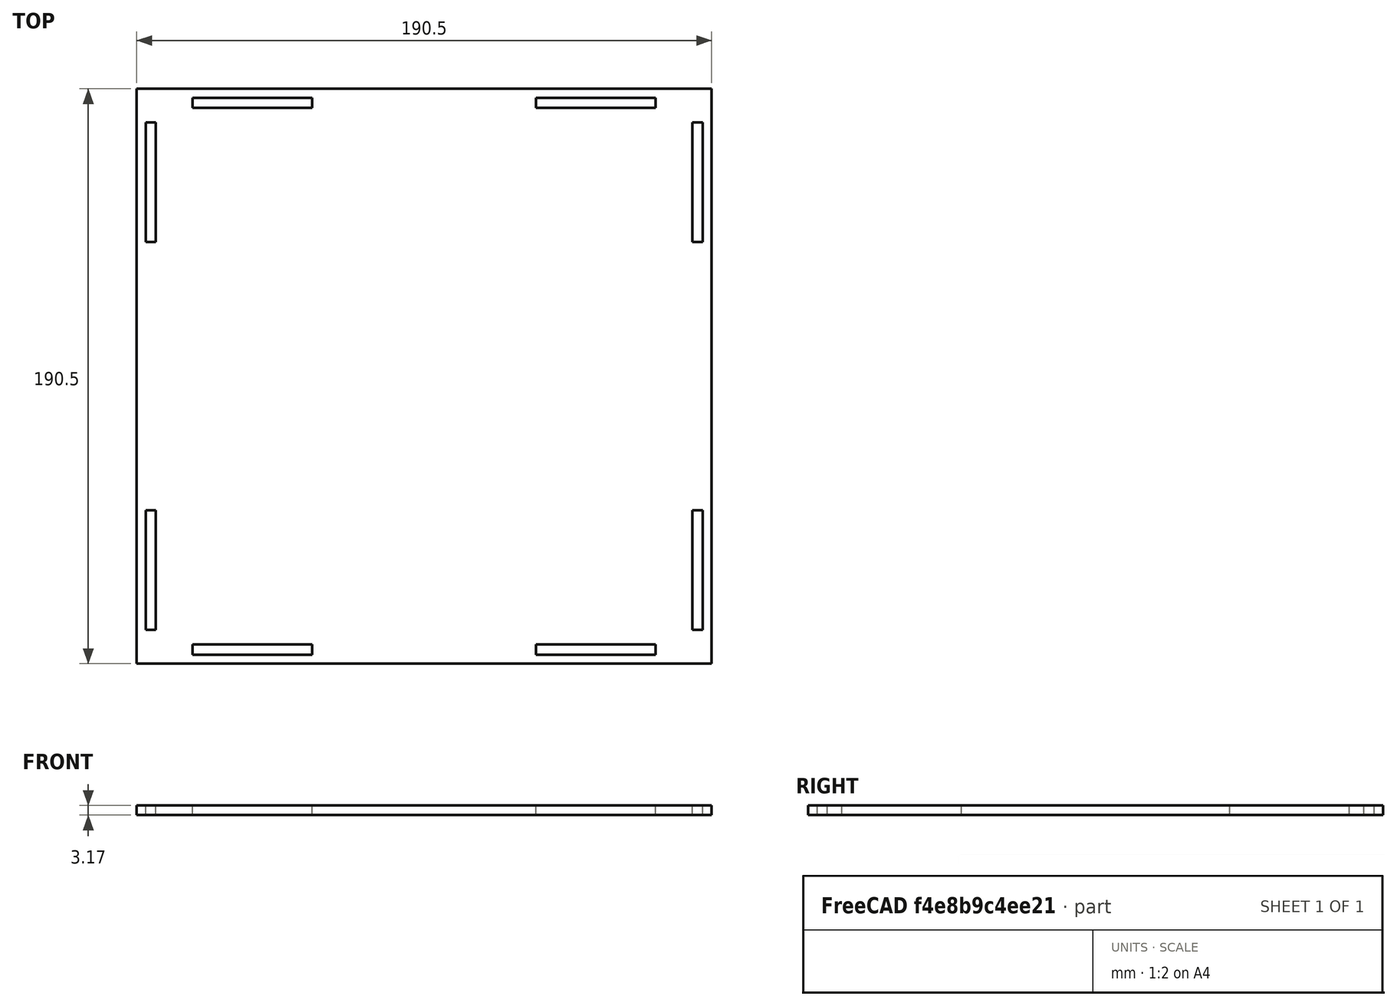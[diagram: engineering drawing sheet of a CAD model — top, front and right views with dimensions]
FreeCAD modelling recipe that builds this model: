
FCSTD DOCUMENT  (FreeCAD 0.18R4 (GitTag))
Label: tpr68k
License: All rights reserved
LicenseURL: http://en.wikipedia.org/wiki/All_rights_reserved
objects: Sketcher::SketchObject×1, PartDesign::Pad×1, PartDesign::Body×1, App::Part×1, Mesh::Feature×1
note: 4 computed .brp shape members not serialized (recipe doc carries the construction recipe); baked Part::Feature solids carry a one-line shape summary decoded from their .brp

FEATURE [Sketcher::SketchObject] Sketch
  MapMode = 5
  Support = -> [XY_Plane001]
  sketch-geometry (36):
    g0: LineSegment StartX=-95.25 StartY=95.25 StartZ=0 EndX=95.25 EndY=95.25 EndZ=0
    g1: LineSegment StartX=95.25 StartY=95.25 StartZ=0 EndX=95.25 EndY=-95.25 EndZ=0
    g2: LineSegment StartX=95.25 StartY=-95.25 StartZ=0 EndX=-95.25 EndY=-95.25 EndZ=0
    g3: LineSegment StartX=-95.25 StartY=-95.25 StartZ=0 EndX=-95.25 EndY=95.25 EndZ=0
    g4: LineSegment StartX=-76.708 StartY=92.2528 StartZ=0 EndX=-37.084 EndY=92.2528 EndZ=0
    g5: LineSegment StartX=-37.084 StartY=92.2528 StartZ=0 EndX=-37.084 EndY=88.9 EndZ=0
    g6: LineSegment StartX=-37.084 StartY=88.9 StartZ=0 EndX=-76.708 EndY=88.9 EndZ=0
    g7: LineSegment StartX=-76.708 StartY=88.9 StartZ=0 EndX=-76.708 EndY=92.2528 EndZ=0
    g8: LineSegment StartX=37.084 StartY=-88.9 StartZ=0 EndX=76.708 EndY=-88.9 EndZ=0
    g9: LineSegment StartX=76.708 StartY=-88.9 StartZ=0 EndX=76.708 EndY=-92.2528 EndZ=0
    g10: LineSegment StartX=76.708 StartY=-92.2528 StartZ=0 EndX=37.084 EndY=-92.2528 EndZ=0
    g11: LineSegment StartX=37.084 StartY=-92.2528 StartZ=0 EndX=37.084 EndY=-88.9 EndZ=0
    g12: LineSegment StartX=-76.708 StartY=-88.9 StartZ=0 EndX=-37.084 EndY=-88.9 EndZ=0
    g13: LineSegment StartX=-37.084 StartY=-88.9 StartZ=0 EndX=-37.084 EndY=-92.2528 EndZ=0
    g14: LineSegment StartX=-37.084 StartY=-92.2528 StartZ=0 EndX=-76.708 EndY=-92.2528 EndZ=0
    g15: LineSegment StartX=-76.708 StartY=-92.2528 StartZ=0 EndX=-76.708 EndY=-88.9 EndZ=0
    g16: LineSegment StartX=37.084 StartY=92.2528 StartZ=0 EndX=76.708 EndY=92.2528 EndZ=0
    g17: LineSegment StartX=76.708 StartY=92.2528 StartZ=0 EndX=76.708 EndY=88.9 EndZ=0
    g18: LineSegment StartX=76.708 StartY=88.9 StartZ=0 EndX=37.084 EndY=88.9 EndZ=0
    g19: LineSegment StartX=37.084 StartY=88.9 StartZ=0 EndX=37.084 EndY=92.2528 EndZ=0
    g20: LineSegment StartX=-92.2528 StartY=84.074 StartZ=0 EndX=-88.9 EndY=84.074 EndZ=0
    g21: LineSegment StartX=-88.9 StartY=84.074 StartZ=0 EndX=-88.9 EndY=44.45 EndZ=0
    g22: LineSegment StartX=-88.9 StartY=44.45 StartZ=0 EndX=-92.2528 EndY=44.45 EndZ=0
    g23: LineSegment StartX=-92.2528 StartY=44.45 StartZ=0 EndX=-92.2528 EndY=84.074 EndZ=0
    g24: LineSegment StartX=88.9 StartY=84.074 StartZ=0 EndX=92.2528 EndY=84.074 EndZ=0
    g25: LineSegment StartX=92.2528 StartY=84.074 StartZ=0 EndX=92.2528 EndY=44.45 EndZ=0
    g26: LineSegment StartX=92.2528 StartY=44.45 StartZ=0 EndX=88.9 EndY=44.45 EndZ=0
    g27: LineSegment StartX=88.9 StartY=44.45 StartZ=0 EndX=88.9 EndY=84.074 EndZ=0
    g28: LineSegment StartX=-92.2528 StartY=-44.45 StartZ=0 EndX=-88.9 EndY=-44.45 EndZ=0
    g29: LineSegment StartX=-88.9 StartY=-44.45 StartZ=0 EndX=-88.9 EndY=-84.074 EndZ=0
    g30: LineSegment StartX=-88.9 StartY=-84.074 StartZ=0 EndX=-92.2528 EndY=-84.074 EndZ=0
    g31: LineSegment StartX=-92.2528 StartY=-84.074 StartZ=0 EndX=-92.2528 EndY=-44.45 EndZ=0
    g32: LineSegment StartX=88.9 StartY=-44.45 StartZ=0 EndX=92.2528 EndY=-44.45 EndZ=0
    g33: LineSegment StartX=92.2528 StartY=-44.45 StartZ=0 EndX=92.2528 EndY=-84.074 EndZ=0
    g34: LineSegment StartX=92.2528 StartY=-84.074 StartZ=0 EndX=88.9 EndY=-84.074 EndZ=0
    g35: LineSegment StartX=88.9 StartY=-84.074 StartZ=0 EndX=88.9 EndY=-44.45 EndZ=0
  constraints (104):
    c: Coincident(g0,g1)
    c: Coincident(g1,g2)
    c: Coincident(g2,g3)
    c: Coincident(g3,g0)
    c: Horizontal(g2)
    c: Vertical(g1)
    c: DistanceY(g2,g0) = 190.5
    c: DistanceX(g0,g0) = 190.5
    c: DistanceY(g-1,g0) = 95.25
    c: DistanceX(g0,g-1) = 95.25
    c: Equal(g0,g2)
    c: Equal(g3,g1)
    c: Coincident(g4,g5)
    c: Coincident(g5,g6)
    c: Coincident(g6,g7)
    c: Coincident(g7,g4)
    c: Horizontal(g4)
    c: Horizontal(g6)
    c: Vertical(g5)
    c: Vertical(g7)
    c: Coincident(g8,g9)
    c: Coincident(g9,g10)
    c: Coincident(g10,g11)
    c: Coincident(g11,g8)
    c: Horizontal(g8)
    c: Horizontal(g10)
    c: Vertical(g9)
    c: Vertical(g11)
    c: Coincident(g12,g13)
    c: Coincident(g13,g14)
    c: Coincident(g14,g15)
    c: Coincident(g15,g12)
    c: Horizontal(g12)
    c: Horizontal(g14)
    c: Vertical(g13)
    c: Vertical(g15)
    c: Coincident(g16,g17)
    c: Coincident(g17,g18)
    c: Coincident(g18,g19)
    c: Coincident(g19,g16)
    c: Horizontal(g16)
    c: Horizontal(g18)
    c: Vertical(g17)
    c: Vertical(g19)
    c: Equal(g7,g11)
    c: Equal(g11,g15)
    c: Equal(g15,g19)
    c: Equal(g4,g8)
    c: Equal(g8,g16)
    c: Equal(g16,g12)
    c: DistanceX(g4,g4) = 39.624
    c: DistanceY(g6,g4) = 3.3528
    c: Symmetric(g5,g8,g-1)
    c: Symmetric(g12,g18,g-1)
    c: Symmetric(g18,g8,g-1)
    c: Symmetric(g5,g18,g-2)
    c: DistanceX(g5,g-1) = 37.084
    c: DistanceY(g-1,g5) = 88.9
    c: Coincident(g20,g21)
    c: Coincident(g21,g22)
    c: Coincident(g22,g23)
    c: Coincident(g23,g20)
    c: Horizontal(g20)
    c: Horizontal(g22)
    c: Vertical(g21)
    c: Vertical(g23)
    c: Coincident(g24,g25)
    c: Coincident(g25,g26)
    c: Coincident(g26,g27)
    c: Coincident(g27,g24)
    c: Horizontal(g24)
    c: Horizontal(g26)
    c: Vertical(g25)
    c: Vertical(g27)
    c: Coincident(g28,g29)
    c: Coincident(g29,g30)
    c: Coincident(g30,g31)
    c: Coincident(g31,g28)
    c: Horizontal(g28)
    c: Horizontal(g30)
    c: Vertical(g29)
    c: Vertical(g31)
    c: Coincident(g32,g33)
    c: Coincident(g33,g34)
    c: Coincident(g34,g35)
    c: Coincident(g35,g32)
    c: Horizontal(g32)
    c: Horizontal(g34)
    c: Vertical(g33)
    c: Vertical(g35)
    c: Equal(g20,g24)
    c: Equal(g24,g28)
    c: Equal(g28,g32)
    c: DistanceX(g20,g20) = 3.3528
    c: Equal(g23,g27)
    c: Equal(g27,g31)
    c: Equal(g31,g35)
    c: DistanceY(g22,g20) = 39.624
    c: Symmetric(g21,g32,g-1)
    c: Symmetric(g28,g26,g-1)
    c: Symmetric(g21,g28,g-1)
    c: Symmetric(g21,g26,g-2)
    c: DistanceX(g21,g-1) = 88.9
    c: DistanceY(g-1,g21) = 44.45
FEATURE [PartDesign::Pad] Pad
  Length = 3.175
  Length2 = 99.9998
  Profile = -> Sketch
  Type = 0
FEATURE [PartDesign::Body] Body
  Group = -> [Sketch,Pad]
  Origin = -> Origin001
  Tip = -> Pad
FEATURE [App::Part] Part
  Group = -> [Body]
  Origin = -> Origin
FEATURE [Mesh::Feature] Mesh  label="tpr68k"
